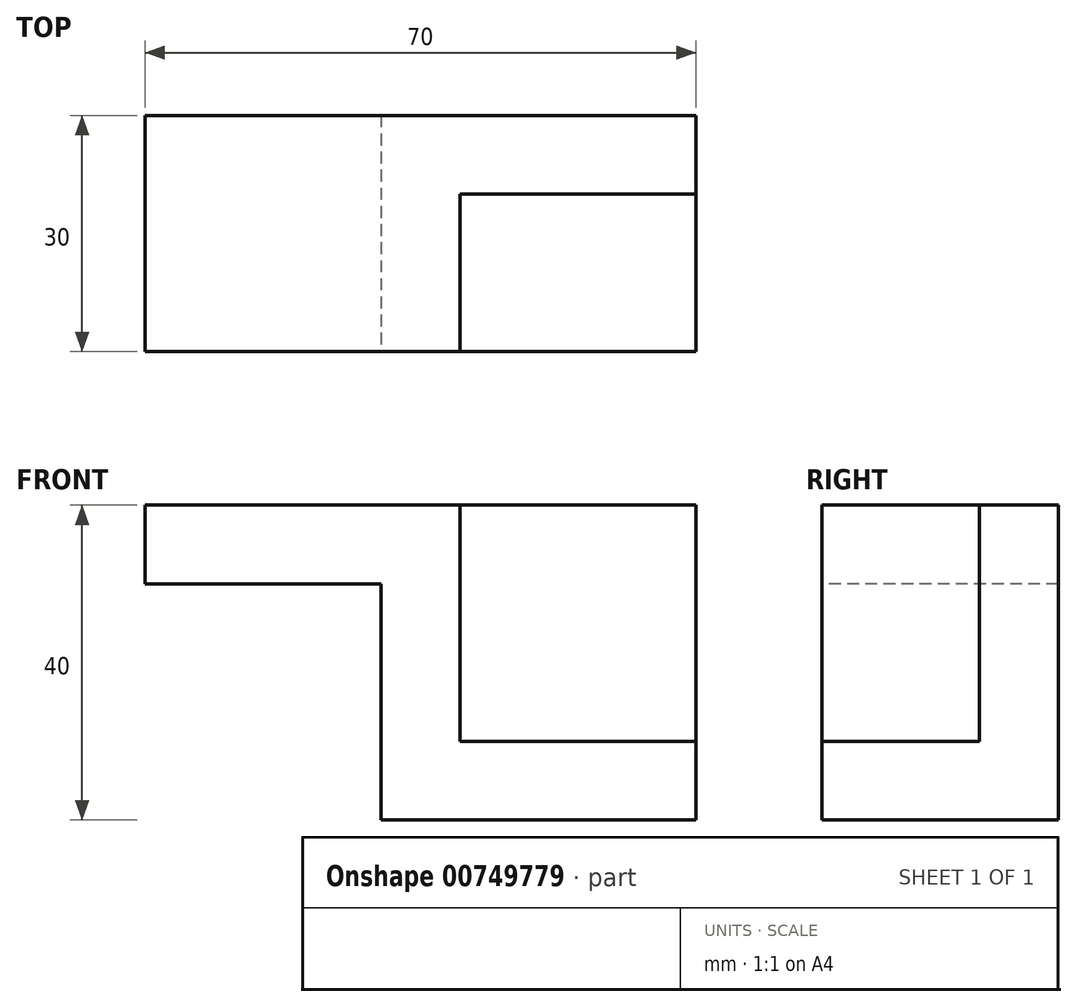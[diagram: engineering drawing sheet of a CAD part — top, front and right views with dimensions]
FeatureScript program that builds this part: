
annotation { "Feature Type Name" : "Feature", "Feature Type Description" : "" }
export const myFeature = defineFeature(function(context is Context, id is Id, definition is map)
    precondition{}
    {
        {
            var Q0;
            Q0=qCreatedBy(makeId("Top.planeOp"),FACE);
            var sketch = newSketch(context, id + "F0", { "sketchPlane" : qUnion([Q0])});
            skLineSegment(sketch, "E0.bottom", {"start": v(0, 0) * mm, "end": v(70, 0) * mm});
            skLineSegment(sketch, "E0.top", {"start": v(0, 30) * mm, "end": v(70, 30) * mm});
            skLineSegment(sketch, "E0.left", {"start": v(0, 0) * mm, "end": v(0, 30) * mm});
            skLineSegment(sketch, "E0.right", {"start": v(70, 0) * mm, "end": v(70, 30) * mm});
            skLineSegment(sketch, "E1.bottom", {"start": v(70, 0) * mm, "end": v(40, 0) * mm});
            skLineSegment(sketch, "E1.top", {"start": v(70, 20) * mm, "end": v(40, 20) * mm});
            skLineSegment(sketch, "E1.left", {"start": v(70, 0) * mm, "end": v(70, 20) * mm});
            skLineSegment(sketch, "E1.right", {"start": v(40, 0) * mm, "end": v(40, 20) * mm});
            skSolve(sketch);
        }
        {
            var Q0;
            {var subQ1=sQuery(id+"F0.wireOp",EDGE,"E0.top");Q0=makeQuery(id+"F0.imprint","IMPRINT",FACE,{"disambiguationData":[TD([[makeQuery(id+"F0.imprint","IMPRINT",EDGE,{"derivedFrom":subQ1}),-1.0]])]});}
            var Q1;
            {var subQ4=sQuery(id+"F0.wireOp",EDGE,"E1.top");Q1=makeQuery(id+"F0.imprint","IMPRINT",FACE,{"disambiguationData":[TD([[makeQuery(id+"F0.imprint","IMPRINT",EDGE,{"derivedFrom":subQ4}),1.0]])]});}
            extrude(context, id + "F1", {"entities" : qUnion([Q0, Q1]), "depth" : 40 * mm, "offsetDistance" : 25 * mm});
        }
        {
            var Q0;
            {var subQ4=sQuery(id+"F0.wireOp",EDGE,"E1.top");Q0=makeQuery(id+"F0.imprint","IMPRINT",FACE,{"disambiguationData":[TD([[makeQuery(id+"F0.imprint","IMPRINT",EDGE,{"derivedFrom":subQ4}),1.0]])]});}
            extrude(context, id + "F2", {"entities" : qUnion([Q0]), "depth" : 10 * mm, "offsetDistance" : 25 * mm});
        }
        {
            var Q0;
            Q0=makeQuery(id+"F2.opExtrude","CAP_FACE",FACE,{"disambiguationData":[OSD([sQuery(id+"F0.wireOp",EDGE,"E0.bottom"),sQuery(id+"F0.wireOp",EDGE,"E0.right"),sQuery(id+"F0.wireOp",EDGE,"E1.top"),sQuery(id+"F0.wireOp",EDGE,"E1.right")])],"isStart":false});
            extrude(context, id + "F3", {"entities" : qUnion([Q0]), "operationType" : NewBodyOperationType.REMOVE, "endBound" : BoundingType.SYMMETRIC, "oppositeDirection" : true, "depth" : 100 * mm, "offsetDistance" : 25 * mm});
        }
        {
            var Q0;
            Q0=makeQuery(id+"F1.opExtrude","SWEPT_FACE",FACE,{"disambiguationData":[OSD([sQuery(id+"F0.wireOp",EDGE,"E0.bottom")])]});
            var sketch = newSketch(context, id + "F4", { "sketchPlane" : qUnion([Q0])});
            skLineSegment(sketch, "E2", {"start": v(0, 0) * mm, "end": v(30, 0) * mm});
            skLineSegment(sketch, "E3", {"start": v(30, 0) * mm, "end": v(30, 30) * mm});
            skLineSegment(sketch, "E4", {"start": v(30, 30) * mm, "end": v(0, 30) * mm});
            skLineSegment(sketch, "E5", {"start": v(0, 30) * mm, "end": v(0, 0) * mm});
            skSolve(sketch);
        }
        {
            var Q0;
            Q0=makeQuery(id+"F4.imprint","IMPRINT",FACE,{"disambiguationData":[TD([[makeQuery(id+"F4.imprint","IMPRINT",EDGE,{"derivedFrom":sQuery(id+"F4.wireOp",EDGE,"E2")}),1.0]])]});
            extrude(context, id + "F5", {"entities" : qUnion([Q0]), "operationType" : NewBodyOperationType.REMOVE, "oppositeDirection" : true, "depth" : 30 * mm, "offsetDistance" : 25 * mm});
        }
        {
            var Q0;
            Q0=makeQuery(id+"F3.boolean.opBoolean","COPY",FACE,{"derivedFrom":makeQuery(id+"F3.opExtrude","SWEPT_FACE",FACE,{"disambiguationData":[OSD([sQuery(id+"F0.wireOp",EDGE,"E1.top")])]})});
            var sketch = newSketch(context, id + "F6", { "sketchPlane" : qUnion([Q0])});
            skLineSegment(sketch, "E6", {"start": v(40, 0) * mm, "end": v(70, 0) * mm});
            skLineSegment(sketch, "E7", {"start": v(70, 0) * mm, "end": v(70, 10) * mm});
            skLineSegment(sketch, "E8", {"start": v(70, 10) * mm, "end": v(40, 10) * mm});
            skLineSegment(sketch, "E9", {"start": v(40, 10) * mm, "end": v(40, 0) * mm});
            skSolve(sketch);
        }
        {
            var Q0;
            Q0=makeQuery(id+"F6.imprint","IMPRINT",FACE,{"disambiguationData":[TD([[makeQuery(id+"F6.imprint","IMPRINT",EDGE,{"derivedFrom":sQuery(id+"F6.wireOp",EDGE,"E6")}),-1.0]])]});
            extrude(context, id + "F7", {"entities" : qUnion([Q0]), "operationType" : NewBodyOperationType.ADD, "depth" : 20 * mm, "offsetDistance" : 25 * mm});
        }
    });
